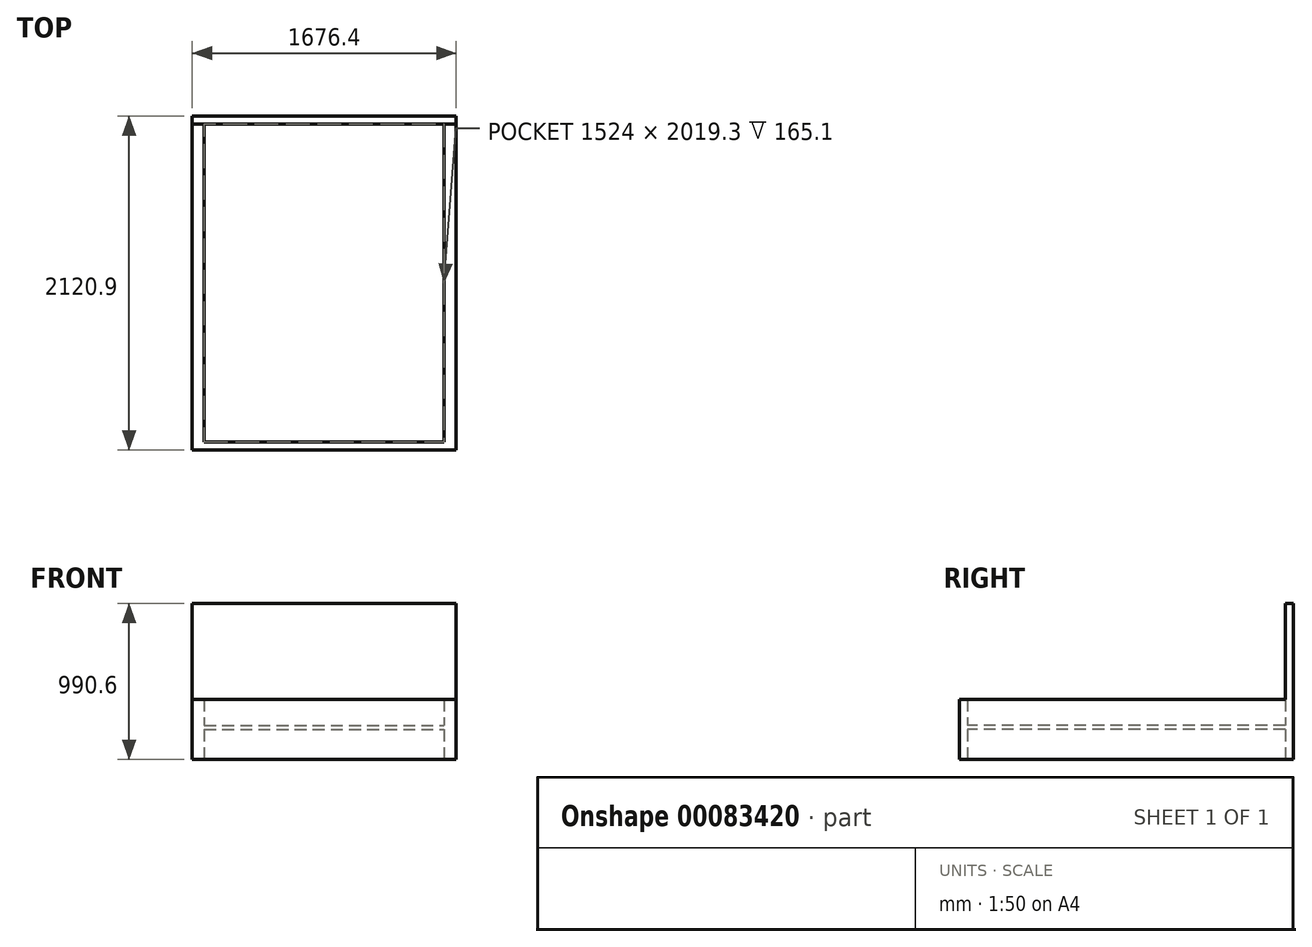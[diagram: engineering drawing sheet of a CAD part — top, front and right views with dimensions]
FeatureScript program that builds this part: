
annotation { "Feature Type Name" : "Feature", "Feature Type Description" : "" }
export const myFeature = defineFeature(function(context is Context, id is Id, definition is map)
    precondition{}
    {
        {
            var Q0;
            Q0=qCreatedBy(makeId("Top.planeOp"),FACE);
            var sketch = newSketch(context, id + "F0", { "sketchPlane" : qUnion([Q0])});
            skLineSegment(sketch, "E0.bottom", {"start": v(-762, 1009.65) * mm, "end": v(762, 1009.65) * mm});
            skLineSegment(sketch, "E0.top", {"start": v(-762, -1009.65) * mm, "end": v(762, -1009.65) * mm});
            skLineSegment(sketch, "E0.left", {"start": v(-762, 1009.65) * mm, "end": v(-762, -1009.65) * mm});
            skLineSegment(sketch, "E0.right", {"start": v(762, 1009.65) * mm, "end": v(762, -1009.65) * mm});
            skPoint(sketch, "E0.middle", {"position": v(0, 0) * mm});
            skLineSegment(sketch, "E1.bottom", {"start": v(-838.2, 1060.45) * mm, "end": v(838.2, 1060.45) * mm});
            skLineSegment(sketch, "E1.top", {"start": v(-838.2, -1060.45) * mm, "end": v(838.2, -1060.45) * mm});
            skLineSegment(sketch, "E1.left", {"start": v(-838.2, 1060.45) * mm, "end": v(-838.2, -1060.45) * mm});
            skLineSegment(sketch, "E1.right", {"start": v(838.2, 1060.45) * mm, "end": v(838.2, -1060.45) * mm});
            skSolve(sketch);
        }
        {
            var Q0;
            Q0=makeQuery(id+"F0.imprint","IMPRINT",FACE,{"disambiguationData":[TD([[makeQuery(id+"F0.imprint","IMPRINT",EDGE,{"derivedFrom":sQuery(id+"F0.wireOp",EDGE,"E0.bottom")}),1.0]])]});
            extrude(context, id + "F1", {"entities" : qUnion([Q0]), "depth" : 190.5 * mm, "hasSecondDirection" : true, "secondDirectionOppositeDirection" : true, "secondDirectionDepth" : 190.5 * mm});
        }
        {
            var Q0;
            Q0=qCreatedBy(makeId("Top.planeOp"),FACE);
            var sketch = newSketch(context, id + "F2", { "sketchPlane" : qUnion([Q0])});
            skLineSegment(sketch, "E2.bottom", {"start": v(-762, 1009.65) * mm, "end": v(762, 1009.65) * mm});
            skLineSegment(sketch, "E2.top", {"start": v(-762, -1009.65) * mm, "end": v(762, -1009.65) * mm});
            skLineSegment(sketch, "E2.left", {"start": v(-762, 1009.65) * mm, "end": v(-762, -1009.65) * mm});
            skLineSegment(sketch, "E2.right", {"start": v(762, 1009.65) * mm, "end": v(762, -1009.65) * mm});
            skPoint(sketch, "E2.middle", {"position": v(0, 0) * mm});
            skSolve(sketch);
        }
        {
            var Q0;
            Q0=makeQuery(id+"F2.imprint","IMPRINT",FACE,{"disambiguationData":[TD([[makeQuery(id+"F2.imprint","IMPRINT",EDGE,{"derivedFrom":sQuery(id+"F2.wireOp",EDGE,"E2.bottom")}),-1.0]])]});
            extrude(context, id + "F3", {"entities" : qUnion([Q0]), "operationType" : NewBodyOperationType.ADD, "depth" : 25.4 * mm});
        }
        {
            var Q0;
            Q0=makeQuery(id+"F1.opExtrude","CAP_FACE",FACE,{"disambiguationData":[OSD([sQuery(id+"F0.wireOp",EDGE,"E0.bottom"),sQuery(id+"F0.wireOp",EDGE,"E0.top"),sQuery(id+"F0.wireOp",EDGE,"E0.left"),sQuery(id+"F0.wireOp",EDGE,"E0.right"),sQuery(id+"F0.wireOp",EDGE,"E1.bottom"),sQuery(id+"F0.wireOp",EDGE,"E1.top"),sQuery(id+"F0.wireOp",EDGE,"E1.left"),sQuery(id+"F0.wireOp",EDGE,"E1.right")])],"isStart":false});
            var sketch = newSketch(context, id + "F4", { "sketchPlane" : qUnion([Q0])});
            skLineSegment(sketch, "E3.bottom", {"start": v(-838.2, 1060.45) * mm, "end": v(838.2, 1060.45) * mm});
            skLineSegment(sketch, "E3.top", {"start": v(-838.2, 1009.65) * mm, "end": v(838.2, 1009.65) * mm});
            skLineSegment(sketch, "E3.left", {"start": v(-838.2, 1060.45) * mm, "end": v(-838.2, 1009.65) * mm});
            skLineSegment(sketch, "E3.right", {"start": v(838.2, 1060.45) * mm, "end": v(838.2, 1009.65) * mm});
            skSolve(sketch);
        }
        {
            var Q0;
            Q0 = qSketchRegion(id + "F4", true);
            extrude(context, id + "F5", {"entities" : qUnion([Q0]), "operationType" : NewBodyOperationType.ADD, "depth" : 609.6 * mm});
        }
    });
